# Revit family: HE-077 Override Switches
name_source: partatom
category: Generic Models
revit_build: Autodesk Revit MEP 2016 (Build: 20150220_1215(x64)
units: mm (PartAtom-declared; Revit-internal decimal feet)

## family parameters
Always vertical = No
Can host rebar = No
Cut with Voids When Loaded = No
OmniClass Number = 23.40.00.00
OmniClass Title = Equipment and Furnishings
Part Type = Normal
Room Calculation Point = No
Round Connector Dimension = Use Diameter
Shared = No
Work Plane-Based = Yes

## types (1)
- Controls
    BIMObject Category_2 = Controls
    BIMobject category = Electrical
    Colour = Orange
    Connection cable = 3 Core
    Cost = 62 $
    Current consumption = 0.1A
    Default Elevation = 1200 mm
    Depth = 35 mm  [stored 0.114829 ft]
    Description = Fireman's override switch to be used with smoke vent systems
    Design country = UK
    Edition number = 1
    Height = 125 mm  [stored 0.410105 ft]
    IFC Classification = Switching Device
    IP rating = IP42
    Manufacturer = Easivent
    Manufacturer URL = http://easivent.co.uk
    Manufacturer country = UK
    Manufacturer name = Easivent
    Material Black Switch = Black Plastic
    Material Main = Plastic Casing - Orange ABS RAL 2011
    Material Secondary = Glass
    Material Switches = Orange  Plastic Switch
    Model = HE-077
    Name of the object = Firemans Override Switch HE-077
    Nominal height = 125
    Nominal width = 125
    Notes = Please note this product may be amended without prior notification
    Product SKU = A3 2122
    Product data URL = http://easivent.co.uk
    Product family = Switches
    Product group = Controls
    SerialNumber = 0
    Size = 125x35x125mm (W x D x H)
    Switch-on-duration_2 = Until manually altered
    TagNumber = 0
    Type Comments = The HE-077 provides a firemans' override facility and can be used for system testing. Each switch comes complete with a plastic enclosure, break glass pane, 3 LED indicators for "Healthy", "Alarm" & "Fault" plus buzzer.
    UNSPSC Code = 39121501
    UNSPSC name = Safety Switches
    Uniclass 2.0 Code = Pr_26_27_50
    Uniclass 2.0 Description = Manual Control Switches
    Uniclass 2015 Code = Pr_75_51_16_66
    Uniclass 2015 Name = Push Button Switches
    Voltage = 24V
    WarrantyDuration = 12
    WarrantyStartDate = From items dispatch
    Weight Net (Kg) = 0.25
    White Plastic = White Plastic
    Width = 125
    switch-on-duration = Until manually adjusted

note: [stored X ft] marks values corroborated as IEEE doubles in the binary element streams (Revit-internal decimal feet)

## geometry (parser evidence)
native form markers: Sweep x7
no freeform markers — native parametric forms only
